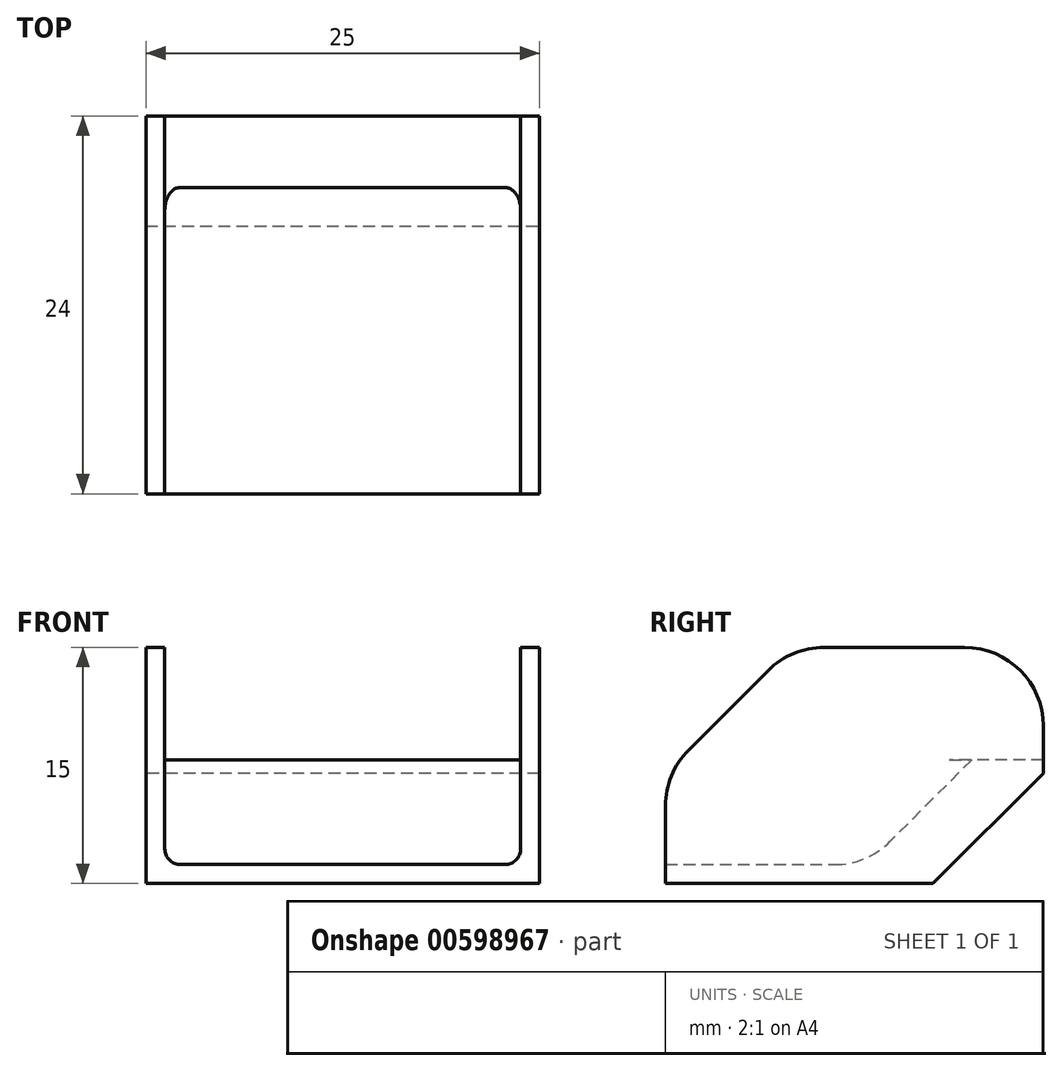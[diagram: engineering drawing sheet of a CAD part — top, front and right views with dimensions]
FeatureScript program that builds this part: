
annotation { "Feature Type Name" : "Feature", "Feature Type Description" : "" }
export const myFeature = defineFeature(function(context is Context, id is Id, definition is map)
    precondition{}
    {
        {
            var Q0;
            Q0=qCreatedBy(makeId("Top.planeOp"),FACE);
            var sketch = newSketch(context, id + "F0", { "sketchPlane" : qUnion([Q0])});
            skLineSegment(sketch, "E0.bottom", {"start": v(-16.6, 0) * mm, "end": v(-41.6, 0) * mm});
            skLineSegment(sketch, "E0.top", {"start": v(-16.6, 24) * mm, "end": v(-41.6, 24) * mm});
            skLineSegment(sketch, "E0.left", {"start": v(-16.6, 0) * mm, "end": v(-16.6, 24) * mm});
            skLineSegment(sketch, "E0.right", {"start": v(-41.6, 0) * mm, "end": v(-41.6, 24) * mm});
            skSolve(sketch);
        }
        {
            var Q0;
            Q0 = qSketchRegion(id + "F0", true);
            extrude(context, id + "F1", {"entities" : qUnion([Q0]), "depth" : 15 * mm, "offsetDistance" : 25 * mm});
        }
        {
            var Q0;
            Q0=makeQuery(id+"F1.opExtrude","CAP_FACE",FACE,{"disambiguationData":[OSD([sQuery(id+"F0.wireOp",EDGE,"E0.bottom"),sQuery(id+"F0.wireOp",EDGE,"E0.top"),sQuery(id+"F0.wireOp",EDGE,"E0.left"),sQuery(id+"F0.wireOp",EDGE,"E0.right")])],"isStart":false});
            shell(context, id + "F2", {"entities" : qUnion([Q0]), "thickness" : 1.2 * mm});
        }
        {
            var Q0;
            Q0=makeQuery(id+"F2.opShell","OFFSET_FACE",FACE,{"disambiguationData":[OSD([sQuery(id+"F0.wireOp",EDGE,"E0.bottom")])]});
            extrude(context, id + "F3", {"entities" : qUnion([Q0]), "operationType" : NewBodyOperationType.REMOVE, "oppositeDirection" : true, "depth" : 25 * mm, "offsetDistance" : 25 * mm});
        }
        {
            var Q0;
            Q0=makeQuery(id+"F2.opShell","OFFSET_FACE",FACE,{"disambiguationData":[OSD([sQuery(id+"F0.wireOp",EDGE,"E0.top")])]});
            var sketch = newSketch(context, id + "F4", { "sketchPlane" : qUnion([Q0])});
            skLineSegment(sketch, "E1.bottom", {"start": v(-40.4, 15) * mm, "end": v(-17.8, 15) * mm});
            skLineSegment(sketch, "E1.top", {"start": v(-40.4, 7.86) * mm, "end": v(-17.8, 7.86) * mm});
            skLineSegment(sketch, "E1.left", {"start": v(-40.4, 15) * mm, "end": v(-40.4, 7.86) * mm});
            skLineSegment(sketch, "E1.right", {"start": v(-17.8, 15) * mm, "end": v(-17.8, 7.86) * mm});
            skSolve(sketch);
        }
        {
            var Q0;
            Q0 = qSketchRegion(id + "F4", true);
            extrude(context, id + "F5", {"entities" : qUnion([Q0]), "operationType" : NewBodyOperationType.REMOVE, "oppositeDirection" : true, "depth" : 25 * mm, "offsetDistance" : 25 * mm});
        }
        {
            var Q0;
            {var subQ0=sQuery(id+"F0.wireOp",EDGE,"E0.top");Q0=makeQuery(id+"F2.opShell","OFFSET_EDGE",EDGE,{"disambiguationData":[OSD([subQ0]),TDD([makeQuery(id+"F1.opExtrude","CAP_EDGE",EDGE,{"disambiguationData":[OSD([subQ0])],"isStart":true})])]});}
            chamfer(context, id + "F6", {"entities" : qUnion([Q0]), "width" : 10 * mm, "tangentPropagation" : true});
        }
        {
            var Q0;
            {var subQ0=sQuery(id+"F0.wireOp",EDGE,"E0.bottom");var subQ1=sQuery(id+"F0.wireOp",EDGE,"E0.top");Q0=makeQuery(id+"F6.opChamfer","BLEND_EDGE",EDGE,{"blendedFrom":[makeQuery(id+"F2.opShell","OFFSET_EDGE",EDGE,{"disambiguationData":[OSD([subQ1]),TDD([makeQuery(id+"F1.opExtrude","CAP_EDGE",EDGE,{"disambiguationData":[OSD([subQ1])],"isStart":true})])]}),makeQuery(id+"F3.boolean.opBoolean","MERGE",FACE,{"derivedFrom":[makeQuery(id+"F2.opShell","OFFSET_FACE",FACE,{"disambiguationData":[OSD([subQ0,subQ1,sQuery(id+"F0.wireOp",EDGE,"E0.left"),sQuery(id+"F0.wireOp",EDGE,"E0.right")])]}),makeQuery(id+"F3.opExtrude","SWEPT_FACE",FACE,{"disambiguationData":[OSD([subQ0]),TDD([makeQuery(id+"F2.opShell","OFFSET_EDGE",EDGE,{"disambiguationData":[OSD([subQ0]),TDD([makeQuery(id+"F1.opExtrude","CAP_EDGE",EDGE,{"disambiguationData":[OSD([subQ0])],"isStart":true})])]})])]})]})],"blendedInto":[makeQuery(id+"F3.boolean.opBoolean","MERGE",FACE,{"derivedFrom":[makeQuery(id+"F2.opShell","OFFSET_FACE",FACE,{"disambiguationData":[OSD([subQ0,subQ1,sQuery(id+"F0.wireOp",EDGE,"E0.left"),sQuery(id+"F0.wireOp",EDGE,"E0.right")])]}),makeQuery(id+"F3.opExtrude","SWEPT_FACE",FACE,{"disambiguationData":[OSD([subQ0]),TDD([makeQuery(id+"F2.opShell","OFFSET_EDGE",EDGE,{"disambiguationData":[OSD([subQ0]),TDD([makeQuery(id+"F1.opExtrude","CAP_EDGE",EDGE,{"disambiguationData":[OSD([subQ0])],"isStart":true})])]})])]})]})]});}
            var Q1;
            {var subQ0=sQuery(id+"F0.wireOp",EDGE,"E0.top");Q1=makeQuery(id+"F6.opChamfer","BLEND_EDGE",EDGE,{"blendedFrom":[makeQuery(id+"F2.opShell","OFFSET_EDGE",EDGE,{"disambiguationData":[OSD([subQ0]),TDD([makeQuery(id+"F1.opExtrude","CAP_EDGE",EDGE,{"disambiguationData":[OSD([subQ0])],"isStart":true})])]}),makeQuery(id+"F2.opShell","OFFSET_FACE",FACE,{"disambiguationData":[OSD([subQ0])]})],"blendedInto":[makeQuery(id+"F2.opShell","OFFSET_FACE",FACE,{"disambiguationData":[OSD([subQ0])]})]});}
            fillet(context, id + "F7", {"entities" : qUnion([Q0, Q1]), "radius" : 5 * mm, "tangentPropagation" : true, "allowEdgeOverflow" : false});
        }
        {
            var Q0;
            {var subQ0=sQuery(id+"F0.wireOp",EDGE,"E0.right");var subQ1=sQuery(id+"F0.wireOp",EDGE,"E0.bottom");Q0=makeQuery(id+"F3.boolean.opBoolean","SPLIT",EDGE,{"disambiguationData":[TD([makeQuery(id+"F1.opExtrude","SWEPT_FACE",FACE,{"disambiguationData":[OSD([subQ0])]})])],"derivedFrom":makeQuery(id+"F1.opExtrude","CAP_EDGE",EDGE,{"disambiguationData":[OSD([subQ1])],"isStart":false})});}
            var Q1;
            {var subQ0=sQuery(id+"F0.wireOp",EDGE,"E0.left");var subQ1=sQuery(id+"F0.wireOp",EDGE,"E0.bottom");Q1=makeQuery(id+"F3.boolean.opBoolean","SPLIT",EDGE,{"disambiguationData":[TD([makeQuery(id+"F1.opExtrude","SWEPT_FACE",FACE,{"disambiguationData":[OSD([subQ0])]})])],"derivedFrom":makeQuery(id+"F1.opExtrude","CAP_EDGE",EDGE,{"disambiguationData":[OSD([subQ1])],"isStart":false})});}
            chamfer(context, id + "F8", {"entities" : qUnion([Q0, Q1]), "width" : 8 * mm, "tangentPropagation" : true});
        }
        {
            var Q0;
            {var subQ0=sQuery(id+"F0.wireOp",EDGE,"E0.top");var subQ1=sQuery(id+"F0.wireOp",EDGE,"E0.right");var subQ3=makeQuery(id+"F1.opExtrude","SWEPT_FACE",FACE,{"disambiguationData":[OSD([subQ1])]});var subQ4=sQuery(id+"F0.wireOp",EDGE,"E0.bottom");var subQ7=makeQuery(id+"F1.opExtrude","CAP_FACE",FACE,{"disambiguationData":[OSD([subQ4,subQ0,sQuery(id+"F0.wireOp",EDGE,"E0.left"),subQ1])],"isStart":false});Q0=makeQuery(id+"F8.opChamfer","BLEND_EDGE",EDGE,{"blendedFrom":[makeQuery(id+"F3.boolean.opBoolean","SPLIT",EDGE,{"disambiguationData":[TD([subQ3])],"derivedFrom":makeQuery(id+"F1.opExtrude","CAP_EDGE",EDGE,{"disambiguationData":[OSD([subQ4])],"isStart":false})}),makeQuery(id+"F5.boolean.opBoolean","SPLIT",FACE,{"disambiguationData":[TD([subQ3])],"derivedFrom":subQ7})],"blendedInto":[makeQuery(id+"F5.boolean.opBoolean","SPLIT",FACE,{"disambiguationData":[TD([subQ3])],"derivedFrom":subQ7})]});}
            var Q1;
            {var subQ0=sQuery(id+"F0.wireOp",EDGE,"E0.bottom");var subQ1=makeQuery(id+"F1.opExtrude","SWEPT_FACE",FACE,{"disambiguationData":[OSD([subQ0])]});var subQ2=sQuery(id+"F0.wireOp",EDGE,"E0.right");Q1=makeQuery(id+"F8.opChamfer","BLEND_EDGE",EDGE,{"blendedFrom":[makeQuery(id+"F3.boolean.opBoolean","SPLIT",EDGE,{"disambiguationData":[TD([makeQuery(id+"F1.opExtrude","SWEPT_FACE",FACE,{"disambiguationData":[OSD([subQ2])]})])],"derivedFrom":makeQuery(id+"F1.opExtrude","CAP_EDGE",EDGE,{"disambiguationData":[OSD([subQ0])],"isStart":false})}),subQ1],"blendedInto":[subQ1]});}
            var Q2;
            {var subQ0=sQuery(id+"F0.wireOp",EDGE,"E0.bottom");var subQ1=makeQuery(id+"F1.opExtrude","SWEPT_FACE",FACE,{"disambiguationData":[OSD([subQ0])]});var subQ2=sQuery(id+"F0.wireOp",EDGE,"E0.left");Q2=makeQuery(id+"F8.opChamfer","BLEND_EDGE",EDGE,{"blendedFrom":[makeQuery(id+"F3.boolean.opBoolean","SPLIT",EDGE,{"disambiguationData":[TD([makeQuery(id+"F1.opExtrude","SWEPT_FACE",FACE,{"disambiguationData":[OSD([subQ2])]})])],"derivedFrom":makeQuery(id+"F1.opExtrude","CAP_EDGE",EDGE,{"disambiguationData":[OSD([subQ0])],"isStart":false})}),subQ1],"blendedInto":[subQ1]});}
            var Q3;
            {var subQ0=sQuery(id+"F0.wireOp",EDGE,"E0.left");var subQ2=makeQuery(id+"F1.opExtrude","SWEPT_FACE",FACE,{"disambiguationData":[OSD([subQ0])]});var subQ3=sQuery(id+"F0.wireOp",EDGE,"E0.top");var subQ4=sQuery(id+"F0.wireOp",EDGE,"E0.bottom");var subQ7=makeQuery(id+"F1.opExtrude","CAP_FACE",FACE,{"disambiguationData":[OSD([subQ4,subQ3,subQ0,sQuery(id+"F0.wireOp",EDGE,"E0.right")])],"isStart":false});Q3=makeQuery(id+"F8.opChamfer","BLEND_EDGE",EDGE,{"blendedFrom":[makeQuery(id+"F3.boolean.opBoolean","SPLIT",EDGE,{"disambiguationData":[TD([subQ2])],"derivedFrom":makeQuery(id+"F1.opExtrude","CAP_EDGE",EDGE,{"disambiguationData":[OSD([subQ4])],"isStart":false})}),makeQuery(id+"F5.boolean.opBoolean","SPLIT",FACE,{"disambiguationData":[TD([subQ2])],"derivedFrom":subQ7})],"blendedInto":[makeQuery(id+"F5.boolean.opBoolean","SPLIT",FACE,{"disambiguationData":[TD([subQ2])],"derivedFrom":subQ7})]});}
            var Q4;
            {var subQ0=sQuery(id+"F0.wireOp",EDGE,"E0.left");var subQ1=sQuery(id+"F0.wireOp",EDGE,"E0.top");Q4=makeQuery(id+"F5.boolean.opBoolean","SPLIT",EDGE,{"disambiguationData":[TD([makeQuery(id+"F1.opExtrude","SWEPT_FACE",FACE,{"disambiguationData":[OSD([subQ0])]})])],"derivedFrom":makeQuery(id+"F1.opExtrude","CAP_EDGE",EDGE,{"disambiguationData":[OSD([subQ1])],"isStart":false})});}
            var Q5;
            {var subQ0=sQuery(id+"F0.wireOp",EDGE,"E0.right");var subQ1=sQuery(id+"F0.wireOp",EDGE,"E0.top");Q5=makeQuery(id+"F5.boolean.opBoolean","SPLIT",EDGE,{"disambiguationData":[TD([makeQuery(id+"F1.opExtrude","SWEPT_FACE",FACE,{"disambiguationData":[OSD([subQ0])]})])],"derivedFrom":makeQuery(id+"F1.opExtrude","CAP_EDGE",EDGE,{"disambiguationData":[OSD([subQ1])],"isStart":false})});}
            fillet(context, id + "F9", {"entities" : qUnion([Q0, Q1, Q2, Q3, Q4, Q5]), "radius" : 5 * mm, "tangentPropagation" : true, "allowEdgeOverflow" : false});
        }
        {
            var Q0;
            {var subQ0=sQuery(id+"F0.wireOp",EDGE,"E0.right");var subQ1=sQuery(id+"F0.wireOp",EDGE,"E0.bottom");Q0=makeQuery(id+"F3.boolean.opBoolean","MERGE",EDGE,{"derivedFrom":[makeQuery(id+"F2.opShell","OFFSET_EDGE",EDGE,{"disambiguationData":[OSD([subQ0]),TDD([makeQuery(id+"F1.opExtrude","CAP_EDGE",EDGE,{"disambiguationData":[OSD([subQ0])],"isStart":true})])]}),makeQuery(id+"F3.opExtrude","SWEPT_EDGE",EDGE,{"disambiguationData":[OSD([subQ1,subQ0]),TDD([makeQuery(id+"F2.opShell","OFFSET_VERTEX",VERTEX,{"disambiguationData":[OSD([subQ1,subQ0]),TDD([makeQuery(id+"F1.opExtrude","CAP_VERTEX",VERTEX,{"disambiguationData":[OSD([subQ1,subQ0])],"isStart":true})])]})])]})]});}
            var Q1;
            {var subQ0=sQuery(id+"F0.wireOp",EDGE,"E0.left");var subQ1=sQuery(id+"F0.wireOp",EDGE,"E0.bottom");Q1=makeQuery(id+"F3.boolean.opBoolean","MERGE",EDGE,{"derivedFrom":[makeQuery(id+"F2.opShell","OFFSET_EDGE",EDGE,{"disambiguationData":[OSD([subQ0]),TDD([makeQuery(id+"F1.opExtrude","CAP_EDGE",EDGE,{"disambiguationData":[OSD([subQ0])],"isStart":true})])]}),makeQuery(id+"F3.opExtrude","SWEPT_EDGE",EDGE,{"disambiguationData":[OSD([subQ1,subQ0]),TDD([makeQuery(id+"F2.opShell","OFFSET_VERTEX",VERTEX,{"disambiguationData":[OSD([subQ1,subQ0]),TDD([makeQuery(id+"F1.opExtrude","CAP_VERTEX",VERTEX,{"disambiguationData":[OSD([subQ1,subQ0])],"isStart":true})])]})])]})]});}
            fillet(context, id + "F10", {"entities" : qUnion([Q0, Q1]), "radius" : 1 * mm, "tangentPropagation" : true, "allowEdgeOverflow" : false});
        }
        {
            var Q0;
            Q0=makeQuery(id+"F1.opExtrude","CAP_EDGE",EDGE,{"disambiguationData":[OSD([sQuery(id+"F0.wireOp",EDGE,"E0.top")])],"isStart":true});
            chamfer(context, id + "F11", {"entities" : qUnion([Q0]), "width" : 7 * mm, "tangentPropagation" : true});
        }
    });
